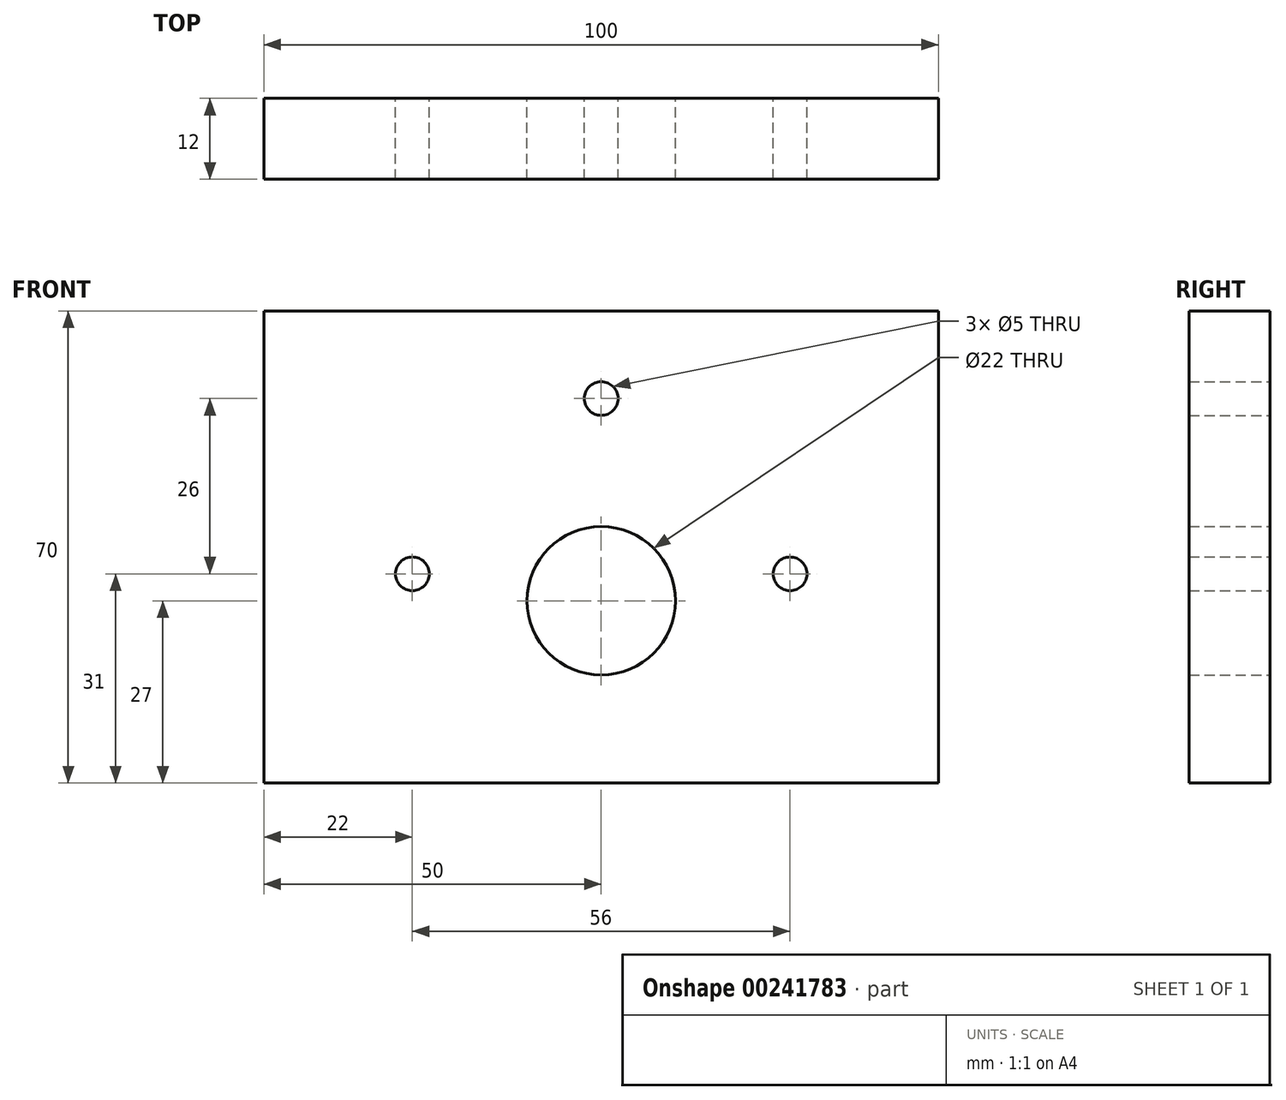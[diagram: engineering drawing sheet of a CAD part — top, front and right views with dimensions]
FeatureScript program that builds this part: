
annotation { "Feature Type Name" : "Feature", "Feature Type Description" : "" }
export const myFeature = defineFeature(function(context is Context, id is Id, definition is map)
    precondition{}
    {
        {
            var Q0;
            Q0=qCreatedBy(makeId("Front.planeOp"),FACE);
            var sketch = newSketch(context, id + "F0", { "sketchPlane" : qUnion([Q0])});
            skLineSegment(sketch, "E0.bottom", {"start": v(0, 0) * mm, "end": v(100, 0) * mm});
            skLineSegment(sketch, "E0.top", {"start": v(0, 70) * mm, "end": v(100, 70) * mm});
            skLineSegment(sketch, "E0.left", {"start": v(0, 0) * mm, "end": v(0, 70) * mm});
            skLineSegment(sketch, "E0.right", {"start": v(100, 0) * mm, "end": v(100, 70) * mm});
            skCircle(sketch, "E1", {"center": v(50, 27) * mm, "radius": 11 * mm});
            skCircle(sketch, "E2", {"center": v(22, 31) * mm, "radius": 2.5 * mm});
            skCircle(sketch, "E3", {"center": v(50, 57) * mm, "radius": 2.5 * mm});
            skCircle(sketch, "E4", {"center": v(78, 31) * mm, "radius": 2.5 * mm});
            skSolve(sketch);
        }
        {
            var Q0;
            Q0=qSketchRegion(id+"F0",true);
            extrude(context, id + "F1", {"entities" : qUnion([Q0]), "depth" : 12 * mm});
        }
    });
